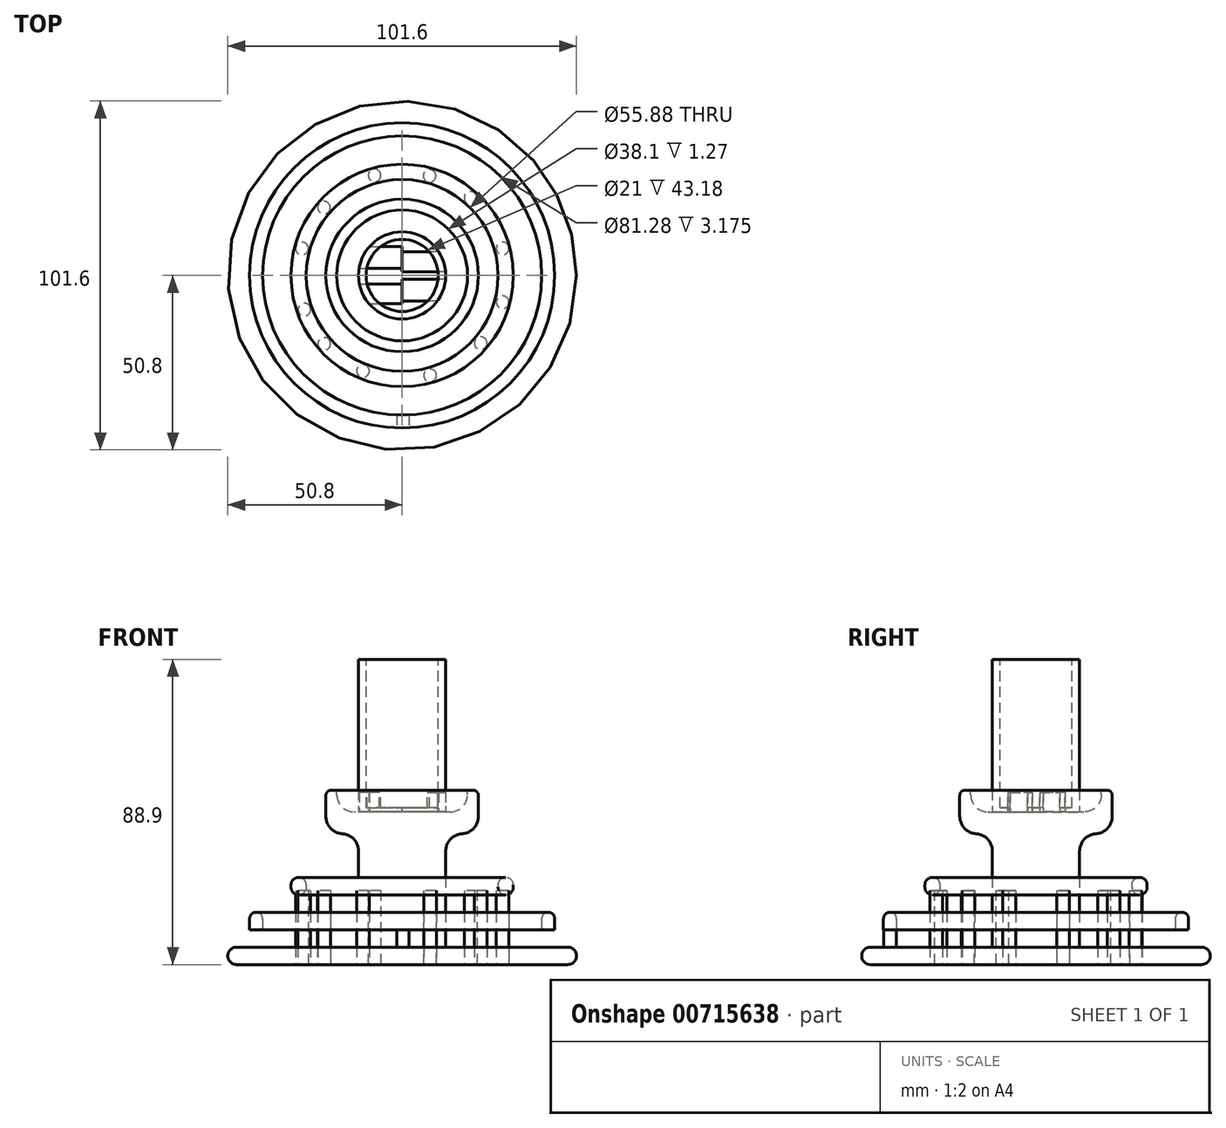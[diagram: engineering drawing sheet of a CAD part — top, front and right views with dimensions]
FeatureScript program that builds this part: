
annotation { "Feature Type Name" : "Feature", "Feature Type Description" : "" }
export const myFeature = defineFeature(function(context is Context, id is Id, definition is map)
    precondition{}
    {
        {
            var Q0;
            Q0=qCreatedBy(makeId("Top.planeOp"),FACE);
            var sketch = newSketch(context, id + "F0", { "sketchPlane" : qUnion([Q0])});
            skCircle(sketch, "E0", {"center": v(0, 0) * mm, "radius": 50.8 * mm});
            skSolve(sketch);
        }
        {
            var Q0;
            Q0=qSketchRegion(id+"F0",true);
            extrude(context, id + "F1", {"entities" : qUnion([Q0]), "depth" : 5.08 * mm, "offsetDistance" : 25.4 * mm});
        }
        {
            var Q0;
            Q0=makeQuery(id+"F1.opExtrude","SWEPT_FACE",FACE,{"disambiguationData":[OSD([sQuery(id+"F0.wireOp",EDGE,"E0")])]});
            fillet(context, id + "F2", {"entities" : qUnion([Q0]), "radius" : 2.54 * mm, "tangentPropagation" : true, "allowEdgeOverflow" : false});
        }
        {
            var Q0;
            Q0=qCreatedBy(makeId("Top.planeOp"),FACE);
            var sketch = newSketch(context, id + "F3", { "sketchPlane" : qUnion([Q0])});
            skCircle(sketch, "E1", {"center": v(0, 0) * mm, "radius": 12.7 * mm});
            skSolve(sketch);
        }
        {
            var Q0;
            Q0=qSketchRegion(id+"F3",true);
            extrude(context, id + "F4", {"entities" : qUnion([Q0]), "operationType" : NewBodyOperationType.ADD, "depth" : 88.9 * mm, "offsetDistance" : 25.4 * mm});
        }
        {
            var Q0;
            Q0=qCreatedBy(makeId("Top.planeOp"),FACE);
            var sketch = newSketch(context, id + "F5", { "sketchPlane" : qUnion([Q0])});
            skCircle(sketch, "E2", {"center": v(0, 0) * mm, "radius": 22.23 * mm});
            skSolve(sketch);
        }
        {
            var Q0;
            Q0=qSketchRegion(id+"F5",true);
            extrude(context, id + "F6", {"entities" : qUnion([Q0]), "operationType" : NewBodyOperationType.ADD, "depth" : 50.8 * mm, "offsetDistance" : 25.4 * mm, "hasSecondDirection" : true, "secondDirectionOppositeDirection" : false, "secondDirectionDepth" : 38.1 * mm});
        }
        {
            var Q0;
            Q0=makeQuery(id+"F6.opExtrude","CAP_EDGE",EDGE,{"disambiguationData":[OSD([sQuery(id+"F5.wireOp",EDGE,"E2")])],"isStart":true});
            fillet(context, id + "F7", {"entities" : qUnion([Q0]), "radius" : 5.08 * mm, "tangentPropagation" : true, "allowEdgeOverflow" : false});
        }
        {
            var Q0;
            Q0=makeQuery(id+"F6.opExtrude","CAP_FACE",FACE,{"disambiguationData":[OSD([sQuery(id+"F5.wireOp",EDGE,"E2")])],"isStart":false});
            var sketch = newSketch(context, id + "F8", { "sketchPlane" : qUnion([Q0])});
            skCircle(sketch, "E3", {"center": v(0, 0) * mm, "radius": 12.7 * mm});
            skCircle(sketch, "E4", {"center": v(0, 0) * mm, "radius": 19.05 * mm});
            skSolve(sketch);
        }
        {
            var Q0;
            Q0=qSketchRegion(id+"F8",true);
            extrude(context, id + "F9", {"entities" : qUnion([Q0]), "operationType" : NewBodyOperationType.REMOVE, "oppositeDirection" : true, "depth" : 6.35 * mm, "offsetDistance" : 25.4 * mm});
        }
        {
            var Q0;
            Q0=makeQuery(id+"F9.boolean.opBoolean","COPY",EDGE,{"derivedFrom":makeQuery(id+"F9.opExtrude","CAP_EDGE",EDGE,{"disambiguationData":[OSD([sQuery(id+"F8.wireOp",EDGE,"E4")])],"isStart":false})});
            fillet(context, id + "F10", {"entities" : qUnion([Q0]), "radius" : 5.08 * mm, "tangentPropagation" : true, "allowEdgeOverflow" : false});
        }
        {
            var Q0;
            Q0=qCreatedBy(makeId("Right.planeOp"),FACE);
            var sketch = newSketch(context, id + "F11", { "sketchPlane" : qUnion([Q0])});
            skLineSegment(sketch, "E5.bottom", {"start": v(-8.18, 44.59) * mm, "end": v(-2.47, 44.59) * mm});
            skLineSegment(sketch, "E5.top", {"start": v(-8.18, 50.22) * mm, "end": v(-2.47, 50.22) * mm});
            skLineSegment(sketch, "E5.left", {"start": v(-8.18, 44.59) * mm, "end": v(-8.18, 50.22) * mm});
            skLineSegment(sketch, "E5.right", {"start": v(-2.47, 44.59) * mm, "end": v(-2.47, 50.22) * mm});
            skLineSegment(sketch, "E6.bottom", {"start": v(2.09, 50.22) * mm, "end": v(8.4, 50.22) * mm});
            skLineSegment(sketch, "E6.top", {"start": v(2.09, 44.67) * mm, "end": v(8.4, 44.67) * mm});
            skLineSegment(sketch, "E6.left", {"start": v(2.09, 50.22) * mm, "end": v(2.09, 44.67) * mm});
            skLineSegment(sketch, "E6.right", {"start": v(8.4, 50.22) * mm, "end": v(8.4, 44.67) * mm});
            skSolve(sketch);
        }
        {
            var Q0;
            Q0=qSketchRegion(id+"F11",true);
            extrude(context, id + "F12", {"entities" : qUnion([Q0]), "operationType" : NewBodyOperationType.REMOVE, "oppositeDirection" : true, "depth" : 12.7 * mm, "offsetDistance" : 25.4 * mm});
        }
        {
            var Q0;
            Q0=qCreatedBy(makeId("Right.planeOp"),FACE);
            var sketch = newSketch(context, id + "F13", { "sketchPlane" : qUnion([Q0])});
            skLineSegment(sketch, "E7.bottom", {"start": v(-7.5, 44.52) * mm, "end": v(-1.1, 44.52) * mm});
            skLineSegment(sketch, "E7.top", {"start": v(-7.5, 50.15) * mm, "end": v(-1.1, 50.15) * mm});
            skLineSegment(sketch, "E7.left", {"start": v(-7.5, 44.52) * mm, "end": v(-7.5, 50.15) * mm});
            skLineSegment(sketch, "E7.right", {"start": v(-1.1, 44.52) * mm, "end": v(-1.1, 50.15) * mm});
            skLineSegment(sketch, "E8.bottom", {"start": v(1.04, 50.15) * mm, "end": v(6.86, 50.15) * mm});
            skLineSegment(sketch, "E8.top", {"start": v(1.04, 44.54) * mm, "end": v(6.86, 44.54) * mm});
            skLineSegment(sketch, "E8.left", {"start": v(1.04, 50.15) * mm, "end": v(1.04, 44.54) * mm});
            skLineSegment(sketch, "E8.right", {"start": v(6.86, 50.15) * mm, "end": v(6.86, 44.54) * mm});
            skSolve(sketch);
        }
        {
            var Q0;
            Q0=qSketchRegion(id+"F13",true);
            extrude(context, id + "F14", {"entities" : qUnion([Q0]), "operationType" : NewBodyOperationType.REMOVE, "depth" : 12.7 * mm, "offsetDistance" : 25.4 * mm});
        }
        {
            var Q0;
            Q0=makeQuery(id+"F4.opExtrude","CAP_FACE",FACE,{"disambiguationData":[OSD([sQuery(id+"F3.wireOp",EDGE,"E1")])],"isStart":false});
            var sketch = newSketch(context, id + "F15", { "sketchPlane" : qUnion([Q0])});
            skCircle(sketch, "E9", {"center": v(0, 0) * mm, "radius": 10.5 * mm});
            skSolve(sketch);
        }
        {
            var Q0;
            Q0=qSketchRegion(id+"F15",true);
            extrude(context, id + "F16", {"entities" : qUnion([Q0]), "operationType" : NewBodyOperationType.REMOVE, "oppositeDirection" : true, "depth" : 43.18 * mm, "offsetDistance" : 25.4 * mm});
        }
        {
            var Q0;
            Q0=makeQuery(id+"F9.boolean.opBoolean","COPY",EDGE,{"derivedFrom":makeQuery(id+"F9.opExtrude","CAP_EDGE",EDGE,{"disambiguationData":[OSD([sQuery(id+"F8.wireOp",EDGE,"E4")])],"isStart":true})});
            var Q1;
            Q1=makeQuery(id+"F6.opExtrude","CAP_EDGE",EDGE,{"disambiguationData":[OSD([sQuery(id+"F5.wireOp",EDGE,"E2")])],"isStart":false});
            fillet(context, id + "F17", {"entities" : qUnion([Q0, Q1]), "radius" : 1.57 * mm, "tangentPropagation" : true, "allowEdgeOverflow" : false});
        }
        {
            var Q0;
            Q0=qCreatedBy(makeId("Top.planeOp"),FACE);
            var sketch = newSketch(context, id + "F18", { "sketchPlane" : qUnion([Q0])});
            skCircle(sketch, "E10", {"center": v(0, 0) * mm, "radius": 32.39 * mm});
            skCircle(sketch, "E11", {"center": v(0, 0) * mm, "radius": 27.94 * mm});
            skSolve(sketch);
        }
        {
            var Q0;
            Q0=qSketchRegion(id+"F18",true);
            extrude(context, id + "F19", {"entities" : qUnion([Q0]), "depth" : 25.4 * mm, "offsetDistance" : 25.4 * mm, "hasSecondDirection" : true, "secondDirectionOppositeDirection" : false, "secondDirectionDepth" : 20.32 * mm});
        }
        {
            var Q0;
            Q0=makeQuery(id+"F19.opExtrude","CAP_EDGE",EDGE,{"disambiguationData":[OSD([sQuery(id+"F18.wireOp",EDGE,"E11")])],"isStart":false});
            var Q1;
            Q1=makeQuery(id+"F19.opExtrude","CAP_FACE",FACE,{"disambiguationData":[OSD([sQuery(id+"F18.wireOp",EDGE,"E10"),sQuery(id+"F18.wireOp",EDGE,"E11")])],"isStart":false});
            var Q2;
            Q2=makeQuery(id+"F19.opExtrude","CAP_EDGE",EDGE,{"disambiguationData":[OSD([sQuery(id+"F18.wireOp",EDGE,"E10")])],"isStart":false});
            var Q3;
            Q3=makeQuery(id+"F19.opExtrude","CAP_EDGE",EDGE,{"disambiguationData":[OSD([sQuery(id+"F18.wireOp",EDGE,"E11")])],"isStart":true});
            var Q4;
            Q4=makeQuery(id+"F19.opExtrude","CAP_EDGE",EDGE,{"disambiguationData":[OSD([sQuery(id+"F18.wireOp",EDGE,"E10")])],"isStart":true});
            fillet(context, id + "F20", {"entities" : qUnion([Q0, Q1, Q2, Q3, Q4]), "radius" : 2.22 * mm, "tangentPropagation" : true, "allowEdgeOverflow" : false});
        }
        {
            var Q0;
            Q0=qCreatedBy(makeId("Top.planeOp"),FACE);
            var sketch = newSketch(context, id + "F21", { "sketchPlane" : qUnion([Q0])});
            skCircle(sketch, "E12", {"center": v(-11.4, -27.8) * mm, "radius": 1.84 * mm});
            skCircle(sketch, "E13", {"center": v(8.15, -29.1) * mm, "radius": 1.84 * mm});
            skCircle(sketch, "E14", {"center": v(22.88, -19.7) * mm, "radius": 1.84 * mm});
            skCircle(sketch, "E15", {"center": v(-22.7, -19.9) * mm, "radius": 1.84 * mm});
            skCircle(sketch, "E16", {"center": v(29.3, -7.8) * mm, "radius": 1.84 * mm});
            skCircle(sketch, "E17", {"center": v(29.3, 7.87) * mm, "radius": 1.84 * mm});
            skCircle(sketch, "E18", {"center": v(19.9, 22.6) * mm, "radius": 1.84 * mm});
            skCircle(sketch, "E19", {"center": v(8, 29.01) * mm, "radius": 1.84 * mm});
            skCircle(sketch, "E20", {"center": v(-8.05, 29.15) * mm, "radius": 1.84 * mm});
            skCircle(sketch, "E21", {"center": v(-22.77, 19.75) * mm, "radius": 1.84 * mm});
            skCircle(sketch, "E22", {"center": v(-29.18, 7.85) * mm, "radius": 1.84 * mm});
            skCircle(sketch, "E23", {"center": v(-28.5, -9.94) * mm, "radius": 1.84 * mm});
            skSolve(sketch);
        }
        {
            var Q0;
            Q0=qSketchRegion(id+"F21",true);
            extrude(context, id + "F22", {"entities" : qUnion([Q0]), "depth" : 21.59 * mm, "offsetDistance" : 25.4 * mm});
        }
        {
            var Q0;
            Q0=qCreatedBy(makeId("Top.planeOp"),FACE);
            var sketch = newSketch(context, id + "F23", { "sketchPlane" : qUnion([Q0])});
            skCircle(sketch, "E24", {"center": v(0, 0) * mm, "radius": 40.64 * mm});
            skCircle(sketch, "E25", {"center": v(0, 0) * mm, "radius": 44.45 * mm});
            skSolve(sketch);
        }
        {
            var Q0;
            Q0=qSketchRegion(id+"F23",true);
            extrude(context, id + "F24", {"entities" : qUnion([Q0]), "depth" : 15.24 * mm, "offsetDistance" : 25.4 * mm, "hasSecondDirection" : true, "secondDirectionOppositeDirection" : false, "secondDirectionDepth" : 10.16 * mm});
        }
        {
            var Q0;
            Q0=makeQuery(id+"F24.opExtrude","CAP_EDGE",EDGE,{"disambiguationData":[OSD([sQuery(id+"F23.wireOp",EDGE,"E24")])],"isStart":false});
            var Q1;
            Q1=makeQuery(id+"F24.opExtrude","CAP_EDGE",EDGE,{"disambiguationData":[OSD([sQuery(id+"F23.wireOp",EDGE,"E25")])],"isStart":false});
            fillet(context, id + "F25", {"entities" : qUnion([Q0, Q1]), "radius" : 1.9 * mm, "tangentPropagation" : true, "allowEdgeOverflow" : false});
        }
        {
            var Q0;
            Q0=makeQuery(id+"F6.boolean.opBoolean","INTERSECT",EDGE,{"derivedFrom":[makeQuery(id+"F4.opExtrude","SWEPT_FACE",FACE,{"disambiguationData":[OSD([sQuery(id+"F3.wireOp",EDGE,"E1")])]}),makeQuery(id+"F6.opExtrude","CAP_FACE",FACE,{"disambiguationData":[OSD([sQuery(id+"F5.wireOp",EDGE,"E2")])],"isStart":true})]});
            fillet(context, id + "F26", {"entities" : qUnion([Q0]), "radius" : 5.08 * mm, "tangentPropagation" : true, "allowEdgeOverflow" : false});
        }
        {
            var Q0;
            Q0=qCreatedBy(makeId("Top.planeOp"),FACE);
            var sketch = newSketch(context, id + "F27", { "sketchPlane" : qUnion([Q0])});
            skLineSegment(sketch, "E26.bottom", {"start": v(-1.6, -40.7) * mm, "end": v(2.02, -40.7) * mm});
            skLineSegment(sketch, "E26.top", {"start": v(-1.6, -44.33) * mm, "end": v(2.02, -44.33) * mm});
            skLineSegment(sketch, "E26.left", {"start": v(-1.6, -40.7) * mm, "end": v(-1.6, -44.33) * mm});
            skLineSegment(sketch, "E26.right", {"start": v(2.02, -40.7) * mm, "end": v(2.02, -44.33) * mm});
            skSolve(sketch);
        }
        {
            var Q0;
            Q0 = qSketchRegion(id + "F27", true);
            extrude(context, id + "F28", {"entities" : qUnion([Q0]), "depth" : 10.16 * mm, "offsetDistance" : 25.4 * mm, "hasSecondDirection" : true, "secondDirectionOppositeDirection" : false, "secondDirectionDepth" : 5.08 * mm});
        }
    });
